# Revit family: 桩基承台-三桩三角形承台
name_source: partatom
category: 结构基础
revit_build: Autodesk Revit 2016 (Build: 20150220_1215(x64)
units: mm (PartAtom-declared; Revit-internal decimal feet)

## family parameters
共享 = 否
加载时剪切的空心 = 否
基于工作平面 = 否
总是垂直 = 是
用于模型行为的材质 = 混凝土
管帽 = 否

## types (2) — shared parameters
D = 300  [stored 0.984252 ft]
S0 = 900  [stored 2.95276 ft]
a1 = 400  [stored 1.31234 ft]
a2 = 400  [stored 1.31234 ft]
桩类型 = 桩 - 混凝土圆形桩 : 300mm 直径
zero-valued in all types: 宽度, 长度

## per-type parameters (varying)
| type | S | S1 | S2 | y | α | 厚度 | 桩嵌固 |
| CT3a-1 | 1200 | 740  [stored 2.42782 ft] | 370  [stored 1.21391 ft] | 1810  [stored 5.93832 ft] | 0.75 | 500  [stored 1.64042 ft] | 100  [stored 0.328084 ft] |
| CT3-1 | 900  [stored 2.95276 ft] | 520  [stored 1.70604 ft] | 260  [stored 0.853018 ft] | 1480  [stored 4.85564 ft] | 1 | 400  [stored 1.31234 ft] | 150 |

note: [stored X ft] marks values corroborated as IEEE doubles in the binary element streams (Revit-internal decimal feet)
